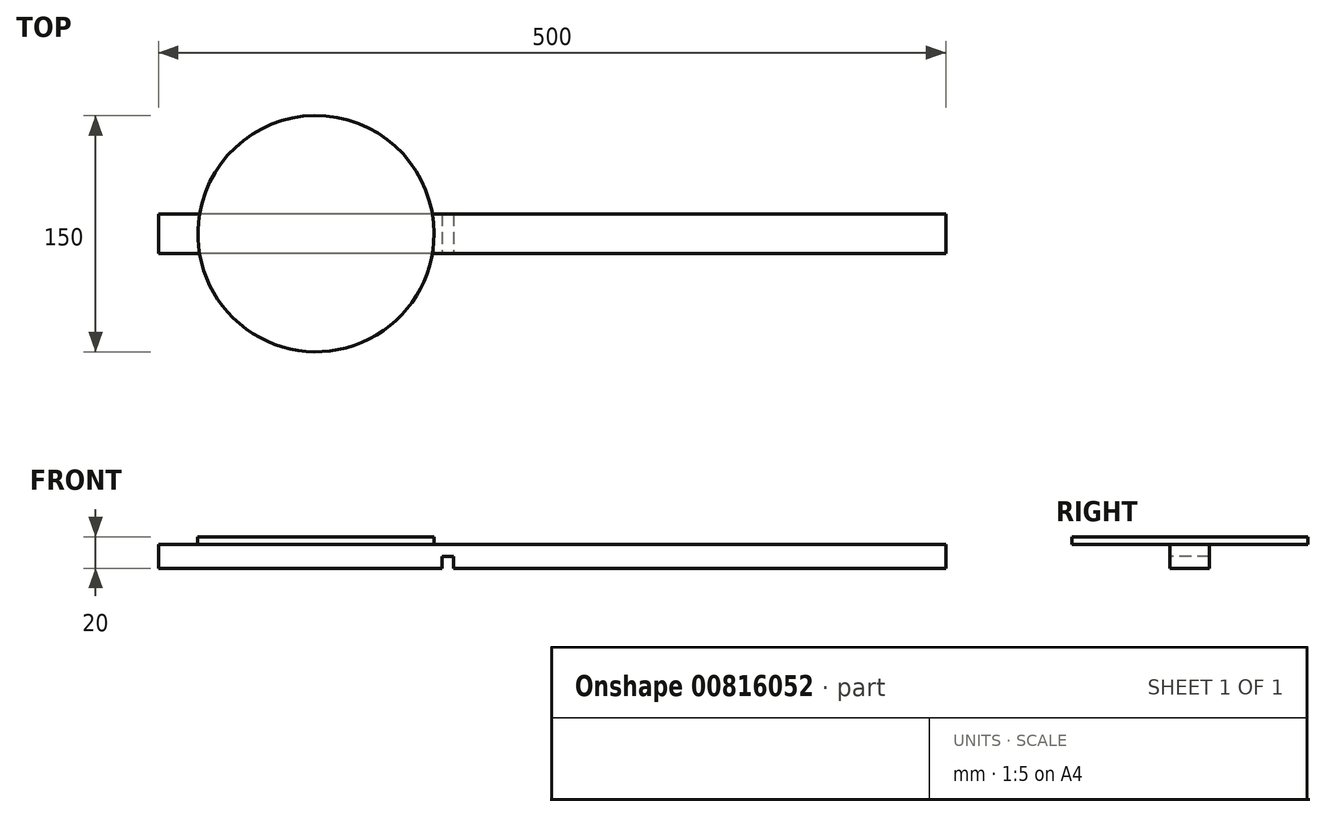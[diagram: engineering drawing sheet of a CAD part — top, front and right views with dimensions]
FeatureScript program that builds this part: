
annotation { "Feature Type Name" : "Feature", "Feature Type Description" : "" }
export const myFeature = defineFeature(function(context is Context, id is Id, definition is map)
    precondition{}
    {
        {
            var Q0;
            Q0=qCreatedBy(makeId("Top.planeOp"),FACE);
            var sketch = newSketch(context, id + "F0", { "sketchPlane" : qUnion([Q0])});
            skLineSegment(sketch, "E0.bottom", {"start": v(0, 12.5) * mm, "end": v(-500, 12.5) * mm});
            skLineSegment(sketch, "E0.top", {"start": v(0, -12.5) * mm, "end": v(-500, -12.5) * mm});
            skLineSegment(sketch, "E0.left", {"start": v(0, 12.5) * mm, "end": v(0, -12.5) * mm});
            skLineSegment(sketch, "E0.right", {"start": v(-500, 12.5) * mm, "end": v(-500, -12.5) * mm});
            skSolve(sketch);
        }
        {
            var Q0;
            Q0=makeQuery(id+"F0.imprint","IMPRINT",FACE,{"disambiguationData":[TD([[makeQuery(id+"F0.imprint","IMPRINT",EDGE,{"derivedFrom":sQuery(id+"F0.wireOp",EDGE,"E0.bottom")}),1.0]])]});
            extrude(context, id + "F1", {"entities" : qUnion([Q0]), "oppositeDirection" : true, "depth" : 15 * mm, "offsetDistance" : 25 * mm});
        }
        {
            var Q0;
            Q0=qCreatedBy(makeId("Top.planeOp"),FACE);
            var sketch = newSketch(context, id + "F2", { "sketchPlane" : qUnion([Q0])});
            skCircle(sketch, "E1", {"center": v(-400, 0) * mm, "radius": 75 * mm});
            skSolve(sketch);
        }
        {
            var Q0;
            Q0=makeQuery(id+"F2.imprint","IMPRINT",FACE,{"disambiguationData":[TD([[makeQuery(id+"F2.imprint","IMPRINT",EDGE,{"derivedFrom":sQuery(id+"F2.wireOp",EDGE,"E1")}),1.0]])]});
            extrude(context, id + "F3", {"entities" : qUnion([Q0]), "operationType" : NewBodyOperationType.ADD, "depth" : 5 * mm, "offsetDistance" : 25 * mm});
        }
        {
            var Q0;
            Q0=qCreatedBy(makeId("Front.planeOp"),FACE);
            var sketch = newSketch(context, id + "F4", { "sketchPlane" : qUnion([Q0])});
            skLineSegment(sketch, "E2.bottom", {"start": v(-320, -15) * mm, "end": v(-312.5, -15) * mm});
            skLineSegment(sketch, "E2.top", {"start": v(-320, -7.5) * mm, "end": v(-312.5, -7.5) * mm});
            skLineSegment(sketch, "E2.left", {"start": v(-320, -15) * mm, "end": v(-320, -7.5) * mm});
            skLineSegment(sketch, "E2.right", {"start": v(-312.5, -15) * mm, "end": v(-312.5, -7.5) * mm});
            skSolve(sketch);
        }
        {
            var Q0;
            Q0=makeQuery(id+"F4.imprint","IMPRINT",FACE,{"disambiguationData":[TD([[makeQuery(id+"F4.imprint","IMPRINT",EDGE,{"derivedFrom":sQuery(id+"F4.wireOp",EDGE,"E2.bottom")}),1.0]])]});
            extrude(context, id + "F5", {"entities" : qUnion([Q0]), "operationType" : NewBodyOperationType.REMOVE, "endBound" : BoundingType.SYMMETRIC, "oppositeDirection" : true, "depth" : 25 * mm, "offsetDistance" : 25 * mm});
        }
    });
